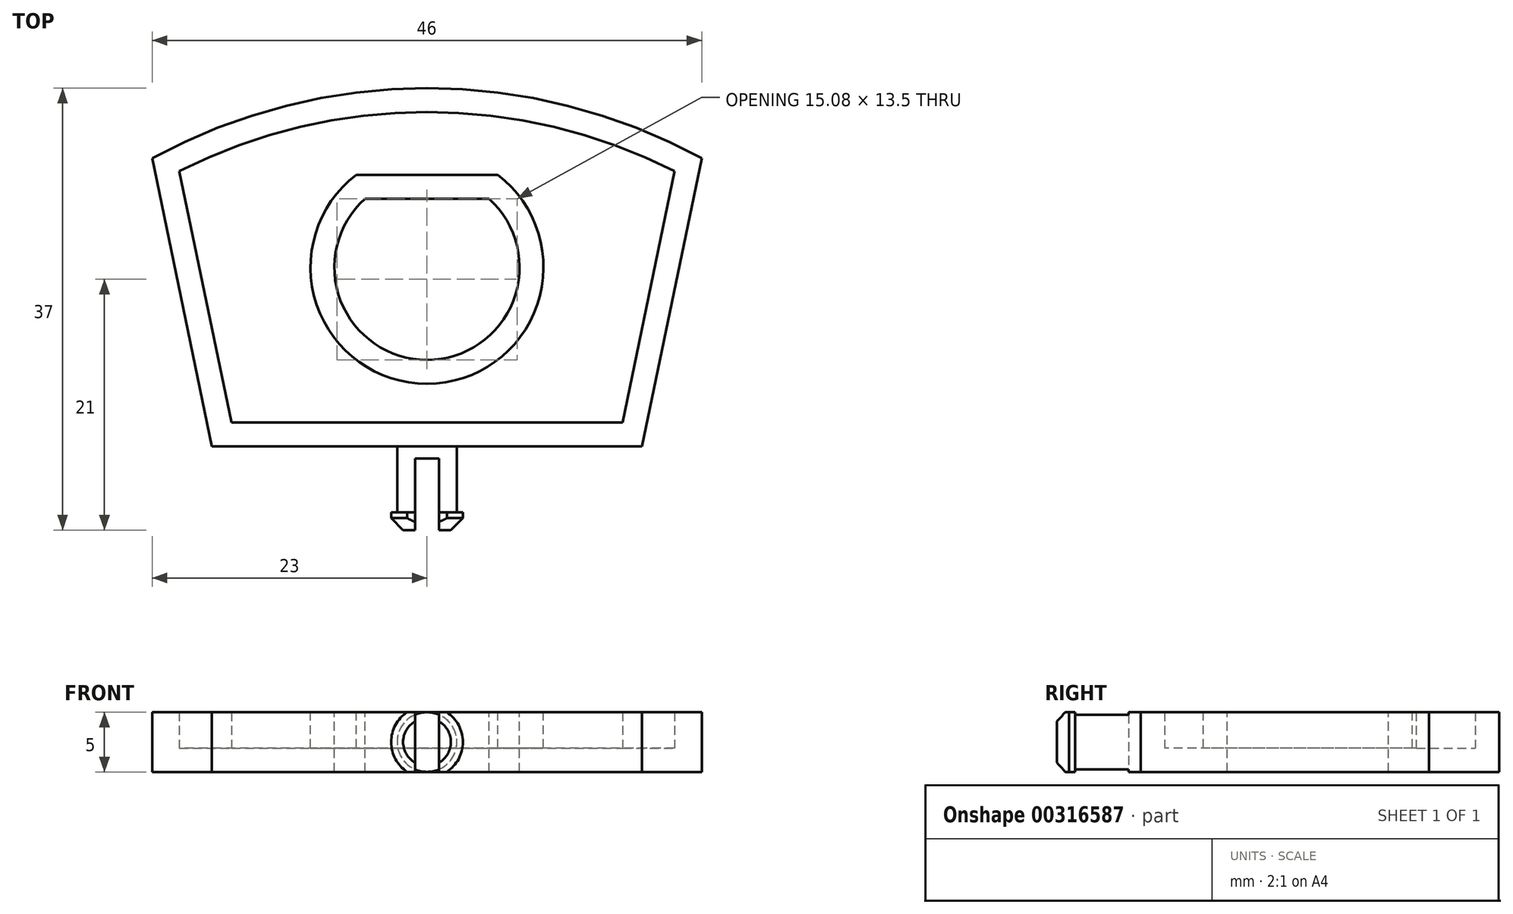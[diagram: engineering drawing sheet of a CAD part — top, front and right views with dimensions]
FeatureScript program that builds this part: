
annotation { "Feature Type Name" : "Feature", "Feature Type Description" : "" }
export const myFeature = defineFeature(function(context is Context, id is Id, definition is map)
    precondition{}
    {
        {
            var Q0;
            Q0=qCreatedBy(makeId("Top.planeOp"),FACE);
            var sketch = newSketch(context, id + "F0", { "sketchPlane" : qUnion([Q0])});
            skLineSegment(sketch, "E0", {"start": v(-23, 24.13) * mm, "end": v(-18, 0) * mm});
            skLineSegment(sketch, "E1", {"start": v(-18, 0) * mm, "end": v(18, 0) * mm});
            skLineSegment(sketch, "E2", {"start": v(18, 0) * mm, "end": v(23, 24.13) * mm});
            skArc(sketch, "E3", {"start": v(23, 24.13) * mm, "mid": v(0, 30) * mm, "end": v(-23, 24.13) * mm});
            skSolve(sketch);
        }
        {
            var Q0;
            Q0 = qSketchRegion(id + "F0", true);
            extrude(context, id + "F1", {"entities" : qUnion([Q0]), "endBound" : BoundingType.SYMMETRIC, "depth" : 5 * mm});
        }
        {
            var Q0;
            Q0=makeQuery(id+"F1.opExtrude","CAP_FACE",FACE,{"disambiguationData":[OSD([sQuery(id+"F0.wireOp",EDGE,"E0"),sQuery(id+"F0.wireOp",EDGE,"E1"),sQuery(id+"F0.wireOp",EDGE,"E2"),sQuery(id+"F0.wireOp",EDGE,"E3")])],"isStart":false});
            var sketch = newSketch(context, id + "F2", { "sketchPlane" : qUnion([Q0])});
            skLineSegment(sketch, "E4", {"start": v(-5.2, 20.75) * mm, "end": v(5.2, 20.75) * mm});
            skArc(sketch, "E5", {"start": v(-5.2, 20.75) * mm, "mid": v(0, 7.25) * mm, "end": v(5.2, 20.75) * mm});
            skSolve(sketch);
        }
        {
            var Q0;
            Q0 = qSketchRegion(id + "F2", true);
            extrude(context, id + "F3", {"entities" : qUnion([Q0]), "operationType" : NewBodyOperationType.REMOVE, "endBound" : BoundingType.UP_TO_NEXT, "oppositeDirection" : true, "depth" : 25 * mm});
        }
        {
            var Q0;
            Q0=makeQuery(id+"F1.opExtrude","CAP_FACE",FACE,{"disambiguationData":[OSD([sQuery(id+"F0.wireOp",EDGE,"E0"),sQuery(id+"F0.wireOp",EDGE,"E1"),sQuery(id+"F0.wireOp",EDGE,"E2"),sQuery(id+"F0.wireOp",EDGE,"E3")])],"isStart":false});
            shell(context, id + "F4", {"entities" : qUnion([Q0]), "thickness" : 2 * mm});
        }
        {
            var Q0;
            Q0=qCreatedBy(makeId("Right.planeOp"),FACE);
            var sketch = newSketch(context, id + "F5", { "sketchPlane" : qUnion([Q0])});
            skLineSegment(sketch, "E6", {"start": v(0, 0) * mm, "end": v(-7, 0) * mm});
            skLineSegment(sketch, "E7", {"start": v(-7, 0) * mm, "end": v(-7, 3) * mm});
            skLineSegment(sketch, "E8", {"start": v(-7, 3) * mm, "end": v(-5.5, 3) * mm});
            skLineSegment(sketch, "E9", {"start": v(-5.5, 3) * mm, "end": v(-5.5, 2.5) * mm});
            skLineSegment(sketch, "E10", {"start": v(-5.5, 2.5) * mm, "end": v(0, 2.5) * mm});
            skLineSegment(sketch, "E11", {"start": v(0, 2.5) * mm, "end": v(0, 0) * mm});
            skSolve(sketch);
        }
        {
            var Q0;
            Q0 = qSketchRegion(id + "F5", true);
            var Q1;
            Q1=sQuery(id+"F5.wireOp",EDGE,"E6");
            revolve(context, id + "F6", {"operationType" : NewBodyOperationType.ADD, "entities" : qUnion([Q0]), "axis" : qUnion([Q1]), "revolveType" : RevolveType.FULL});
        }
        {
            var Q0;
            Q0=makeQuery(id+"F6.opRevolve","SWEPT_EDGE",EDGE,{"disambiguationData":[OSD([sQuery(id+"F5.wireOp",EDGE,"E7"),sQuery(id+"F5.wireOp",EDGE,"E8")])]});
            chamfer(context, id + "F7", {"entities" : qUnion([Q0]), "width" : 1 * mm, "tangentPropagation" : true});
        }
        {
            var Q0;
            Q0=makeQuery(id+"F6.opRevolve","SWEPT_FACE",FACE,{"disambiguationData":[OSD([sQuery(id+"F5.wireOp",EDGE,"E7")])]});
            var sketch = newSketch(context, id + "F8", { "sketchPlane" : qUnion([Q0])});
            skLineSegment(sketch, "E12.bottom", {"start": v(-24.13, -2.5) * mm, "end": v(24.16, -2.5) * mm});
            skLineSegment(sketch, "E12.top", {"start": v(-24.13, 2.5) * mm, "end": v(24.16, 2.5) * mm});
            skLineSegment(sketch, "E12.left", {"start": v(-24.13, -2.5) * mm, "end": v(-24.13, 2.5) * mm});
            skLineSegment(sketch, "E12.right", {"start": v(24.16, -2.5) * mm, "end": v(24.16, 2.5) * mm});
            skSolve(sketch);
        }
        {
            var Q0;
            Q0 = qSketchRegion(id + "F8", true);
            extrude(context, id + "F9", {"entities" : qUnion([Q0]), "operationType" : NewBodyOperationType.INTERSECT, "endBound" : BoundingType.THROUGH_ALL, "oppositeDirection" : true, "depth" : 25 * mm});
        }
        {
            var Q0;
            Q0=makeQuery(id+"F6.opRevolve","SWEPT_FACE",FACE,{"disambiguationData":[OSD([sQuery(id+"F5.wireOp",EDGE,"E7")])]});
            var sketch = newSketch(context, id + "F10", { "sketchPlane" : qUnion([Q0])});
            skLineSegment(sketch, "E13.bottom", {"start": v(-1, 3.08) * mm, "end": v(1, 3.08) * mm});
            skLineSegment(sketch, "E13.top", {"start": v(-1, -3.07) * mm, "end": v(1, -3.07) * mm});
            skLineSegment(sketch, "E13.left", {"start": v(-1, 3.08) * mm, "end": v(-1, -3.07) * mm});
            skLineSegment(sketch, "E13.right", {"start": v(1, 3.08) * mm, "end": v(1, -3.07) * mm});
            skSolve(sketch);
        }
        {
            var Q0;
            Q0 = qSketchRegion(id + "F10", true);
            extrude(context, id + "F11", {"entities" : qUnion([Q0]), "operationType" : NewBodyOperationType.REMOVE, "oppositeDirection" : true, "depth" : 6 * mm});
        }
    });
